# Revit family: НЕВАТОМ_Рама монтажная для ВР-280-46, Версия 1
name_source: partatom
category: Оборудование
revit_build: Autodesk Revit 2017 (Build: 20170118_1100(x64)
units: mm (PartAtom-declared; Revit-internal decimal feet)

## family parameters
Всегда вертикально = Да
На основе рабочей плоскости = Нет
Общий = Нет
При загрузке вырезать с полостями = Нет
Размер круглого соединителя = Использовать диаметр
Тип детали = Нормальный
Точка расчета площади = Нет

## types (1)
- Рама монтажная для ВР-280-46
    ADSK_Единица измерения = шт.
    ADSK_Завод-изготовитель = НЕВАТОМ
    ADSK_Количество = 1
    ADSK_Марка = Монтажная рама для ВР-280-46-8.0
    ADSK_Масса = 40.8
    ADSK_Наименование = Монтажная рама для ВР-280-46-8.0
    C = 1028 мм
    D = 15 мм
    H = 75 мм
    H1 = 74 мм
    L = 115 мм
    Ld = 1180 мм
    Ld1 = 20 мм
    Lh = 1280 мм
    Lm = 968 мм
    Ln = 1265 мм
    Ls = 966 мм
    VR = 8 мм
    a = 24 мм
    t = 1.5 мм
    Материал = Углиродистая сталь ст.3
    Рама = НЕВАТОМ_Рама монтажная для ВР-280-46
